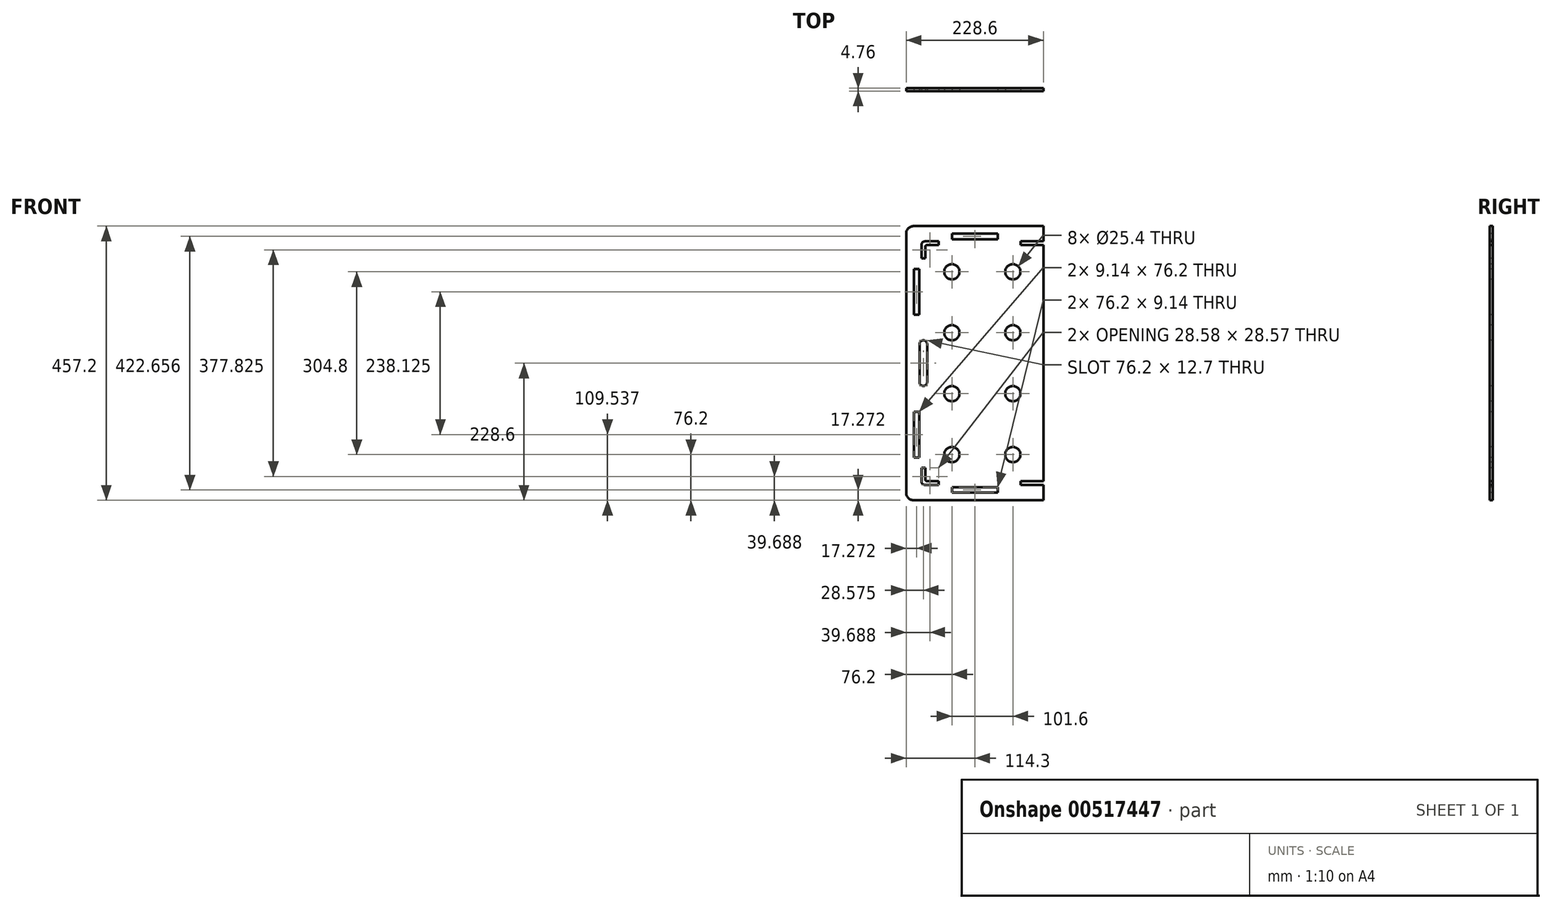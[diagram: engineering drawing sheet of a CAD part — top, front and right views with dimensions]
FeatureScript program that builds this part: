
annotation { "Feature Type Name" : "Feature", "Feature Type Description" : "" }
export const myFeature = defineFeature(function(context is Context, id is Id, definition is map)
    precondition{}
    {
        {
            var Q0;
            Q0=qCreatedBy(makeId("Front.planeOp"),FACE);
            var sketch = newSketch(context, id + "F0", { "sketchPlane" : qUnion([Q0])});
            skLineSegment(sketch, "E0.bottom", {"start": v(114.3, -228.6) * mm, "end": v(-101.6, -228.6) * mm});
            skLineSegment(sketch, "E0.top", {"start": v(114.3, 228.6) * mm, "end": v(-101.6, 228.6) * mm});
            skLineSegment(sketch, "E0.left", {"start": v(114.3, -228.6) * mm, "end": v(114.3, 228.6) * mm});
            skLineSegment(sketch, "E0.right", {"start": v(-114.3, -215.9) * mm, "end": v(-114.3, 215.9) * mm});
            skPoint(sketch, "E0.middle", {"position": v(0, 0) * mm});
            skPoint(sketch, "E1.visualSharp", {"position": v(-114.3, 228.6) * mm});
            skArc(sketch, "E1.filletArc", {"start": v(-101.6, 228.6) * mm, "mid": v(-110.58, 224.88) * mm, "end": v(-114.3, 215.9) * mm});
            skPoint(sketch, "E2.visualSharp", {"position": v(-114.3, -228.6) * mm});
            skArc(sketch, "E2.filletArc", {"start": v(-114.3, -215.9) * mm, "mid": v(-110.58, -224.88) * mm, "end": v(-101.6, -228.6) * mm});
            skSolve(sketch);
        }
        {
            var Q0;
            Q0 = qSketchRegion(id + "F0", true);
            extrude(context, id + "F1", {"entities" : qUnion([Q0]), "depth" : 4.76 * mm, "offsetDistance" : 25.4 * mm});
        }
        {
            var Q0;
            Q0=makeQuery(id+"F1.opExtrude","CAP_FACE",FACE,{"disambiguationData":[OSD([sQuery(id+"F0.wireOp",EDGE,"E0.bottom"),sQuery(id+"F0.wireOp",EDGE,"E0.top"),sQuery(id+"F0.wireOp",EDGE,"E0.left"),sQuery(id+"F0.wireOp",EDGE,"E0.right")])],"isStart":false});
            var sketch = newSketch(context, id + "F2", { "sketchPlane" : qUnion([Q0])});
            skLineSegment(sketch, "E3.MirrorCS", {"start": v(-38.1, -215.9) * mm, "end": v(-38.1, -206.76) * mm});
            skLineSegment(sketch, "E4.MirrorCS", {"start": v(38.1, -215.9) * mm, "end": v(38.1, -206.76) * mm});
            skCircle(sketch, "E5", {"center": v(-38.1, 152.4) * mm, "radius": 12.7 * mm});
            skCircle(sketch, "E6.0.1.0", {"center": v(-38.1, 50.8) * mm, "radius": 12.7 * mm});
            skCircle(sketch, "E6.1.0.0", {"center": v(63.5, 152.4) * mm, "radius": 12.7 * mm});
            skCircle(sketch, "E6.1.1.0", {"center": v(63.5, 50.8) * mm, "radius": 12.7 * mm});
            skLineSegment(sketch, "E6.direction1", {"start": v(-38.1, 152.4) * mm, "end": v(63.5, 152.4) * mm, "construction": true});
            skLineSegment(sketch, "E6.direction2", {"start": v(-38.1, 152.4) * mm, "end": v(-38.1, 50.8) * mm, "construction": true});
            skLineSegment(sketch, "E7", {"start": v(-114.3, 0) * mm, "end": v(114.3, 0) * mm, "construction": true});
            skLineSegment(sketch, "E8.MirrorCS", {"start": v(-92.46, -80.96) * mm, "end": v(-101.6, -80.96) * mm});
            skLineSegment(sketch, "E9.MirrorCS", {"start": v(-92.46, -157.16) * mm, "end": v(-101.6, -157.16) * mm});
            skLineSegment(sketch, "E10.MirrorCS", {"start": v(-101.6, -157.16) * mm, "end": v(-101.6, -80.96) * mm});
            skLineSegment(sketch, "E11", {"start": v(6.35, 228.6) * mm, "end": v(6.35, -228.6) * mm, "construction": true});
            skLineSegment(sketch, "E12.trimOffspring", {"start": v(-38.1, -206.76) * mm, "end": v(38.1, -206.76) * mm});
            skLineSegment(sketch, "E13.trimOffspring", {"start": v(-38.1, -215.9) * mm, "end": v(38.1, -215.9) * mm});
            skLineSegment(sketch, "E14.bottom", {"start": v(114.3, -203.2) * mm, "end": v(76.2, -203.2) * mm});
            skLineSegment(sketch, "E14.top", {"start": v(114.3, -196.85) * mm, "end": v(76.2, -196.85) * mm});
            skLineSegment(sketch, "E14.left", {"start": v(114.3, -203.2) * mm, "end": v(114.3, -196.85) * mm});
            skLineSegment(sketch, "E14.right", {"start": v(76.2, -203.2) * mm, "end": v(76.2, -196.85) * mm});
            skLineSegment(sketch, "E15.bottom", {"start": v(-82.55, -203.2) * mm, "end": v(-60.32, -203.2) * mm});
            skLineSegment(sketch, "E15.top", {"start": v(-79.37, -196.85) * mm, "end": v(-60.32, -196.85) * mm});
            skLineSegment(sketch, "E15.right", {"start": v(-60.32, -203.2) * mm, "end": v(-60.32, -196.85) * mm});
            skLineSegment(sketch, "E16.top", {"start": v(-88.9, -174.63) * mm, "end": v(-82.55, -174.63) * mm});
            skLineSegment(sketch, "E16.left", {"start": v(-88.9, -196.85) * mm, "end": v(-88.9, -174.63) * mm});
            skLineSegment(sketch, "E16.right", {"start": v(-82.55, -193.68) * mm, "end": v(-82.55, -174.63) * mm});
            skCircle(sketch, "E17.MirrorC", {"center": v(-38.1, -50.8) * mm, "radius": 12.7 * mm});
            skCircle(sketch, "E18.MirrorC", {"center": v(63.5, -50.8) * mm, "radius": 12.7 * mm});
            skCircle(sketch, "E19.MirrorC", {"center": v(-38.1, -152.4) * mm, "radius": 12.7 * mm});
            skCircle(sketch, "E20.MirrorC", {"center": v(63.5, -152.4) * mm, "radius": 12.7 * mm});
            skLineSegment(sketch, "E21.bottom", {"start": v(-85.72, -38.1) * mm, "end": v(-85.72, -38.1) * mm});
            skLineSegment(sketch, "E21.right", {"start": v(-79.38, -31.75) * mm, "end": v(-79.38, 31.75) * mm});
            skLineSegment(sketch, "E22", {"start": v(-85.72, 38.1) * mm, "end": v(-85.72, 38.1) * mm});
            skLineSegment(sketch, "E23.trimOffspring", {"start": v(-92.07, -31.75) * mm, "end": v(-92.07, 31.75) * mm});
            skPoint(sketch, "E24.visualSharp", {"position": v(-92.07, 38.1) * mm});
            skArc(sketch, "E24.filletArc", {"start": v(-85.72, 38.1) * mm, "mid": v(-90.22, 36.24) * mm, "end": v(-92.07, 31.75) * mm});
            skPoint(sketch, "E25.visualSharp", {"position": v(-79.38, 38.1) * mm});
            skArc(sketch, "E25.filletArc", {"start": v(-79.37, 31.75) * mm, "mid": v(-81.23, 36.24) * mm, "end": v(-85.72, 38.1) * mm});
            skPoint(sketch, "E26.visualSharp", {"position": v(-79.38, -38.1) * mm});
            skArc(sketch, "E26.filletArc", {"start": v(-85.72, -38.1) * mm, "mid": v(-81.23, -36.24) * mm, "end": v(-79.37, -31.75) * mm});
            skPoint(sketch, "E27.visualSharp", {"position": v(-92.08, -38.1) * mm});
            skArc(sketch, "E27.filletArc", {"start": v(-92.07, -31.75) * mm, "mid": v(-90.22, -36.24) * mm, "end": v(-85.72, -38.1) * mm});
            skLineSegment(sketch, "E28", {"start": v(-92.46, -80.96) * mm, "end": v(-92.46, -157.16) * mm});
            skLineSegment(sketch, "E29.MirrorCS", {"start": v(-92.46, 80.96) * mm, "end": v(-101.6, 80.96) * mm});
            skLineSegment(sketch, "E30.MirrorCS", {"start": v(-92.46, 157.16) * mm, "end": v(-101.6, 157.16) * mm});
            skLineSegment(sketch, "E31.MirrorCS", {"start": v(-101.6, 157.16) * mm, "end": v(-101.6, 80.96) * mm});
            skLineSegment(sketch, "E32.MirrorCS", {"start": v(-92.46, 80.96) * mm, "end": v(-92.46, 157.16) * mm});
            skLineSegment(sketch, "E33.MirrorCS", {"start": v(76.2, 203.2) * mm, "end": v(76.2, 196.85) * mm});
            skLineSegment(sketch, "E34.MirrorCS", {"start": v(6.35, -228.6) * mm, "end": v(6.35, 228.6) * mm, "construction": true});
            skLineSegment(sketch, "E35.MirrorCS", {"start": v(-38.1, 206.76) * mm, "end": v(38.1, 206.76) * mm});
            skLineSegment(sketch, "E36.MirrorCS", {"start": v(38.1, 215.9) * mm, "end": v(38.1, 206.76) * mm});
            skLineSegment(sketch, "E37.MirrorCS", {"start": v(114.3, 203.2) * mm, "end": v(76.2, 203.2) * mm});
            skLineSegment(sketch, "E38.MirrorCS", {"start": v(114.3, 203.2) * mm, "end": v(114.3, 196.85) * mm});
            skLineSegment(sketch, "E39.MirrorCS", {"start": v(-38.1, 215.9) * mm, "end": v(38.1, 215.9) * mm});
            skLineSegment(sketch, "E40.MirrorCS", {"start": v(-38.1, 215.9) * mm, "end": v(-38.1, 206.76) * mm});
            skLineSegment(sketch, "E41.MirrorCS", {"start": v(114.3, 196.85) * mm, "end": v(76.2, 196.85) * mm});
            skPoint(sketch, "E42.visualSharp", {"position": v(-88.9, -203.2) * mm});
            skArc(sketch, "E42.filletArc", {"start": v(-88.9, -196.85) * mm, "mid": v(-87.04, -201.34) * mm, "end": v(-82.55, -203.2) * mm});
            skArc(sketch, "E43.filletArc", {"start": v(-82.55, -193.68) * mm, "mid": v(-81.62, -195.92) * mm, "end": v(-79.37, -196.85) * mm});
            skArc(sketch, "E44.MirrorCS", {"start": v(-82.55, 193.68) * mm, "mid": v(-81.62, 195.92) * mm, "end": v(-79.37, 196.85) * mm});
            skLineSegment(sketch, "E45.MirrorCS", {"start": v(-79.37, 196.85) * mm, "end": v(-60.32, 196.85) * mm});
            skLineSegment(sketch, "E46.MirrorCS", {"start": v(-88.9, 196.85) * mm, "end": v(-88.9, 174.63) * mm});
            skArc(sketch, "E47.MirrorCS", {"start": v(-88.9, 196.85) * mm, "mid": v(-87.04, 201.34) * mm, "end": v(-82.55, 203.2) * mm});
            skLineSegment(sketch, "E48.MirrorCS", {"start": v(-82.55, 203.2) * mm, "end": v(-60.32, 203.2) * mm});
            skLineSegment(sketch, "E49.MirrorCS", {"start": v(-82.55, 193.68) * mm, "end": v(-82.55, 174.63) * mm});
            skLineSegment(sketch, "E50.MirrorCS", {"start": v(-60.32, 203.2) * mm, "end": v(-60.32, 196.85) * mm});
            skLineSegment(sketch, "E51.MirrorCS", {"start": v(-88.9, 174.63) * mm, "end": v(-82.55, 174.63) * mm});
            skPoint(sketch, "E52.MirrorP", {"position": v(-88.9, 203.2) * mm});
            skPoint(sketch, "E53", {"position": v(76.2, -200.03) * mm});
            skPoint(sketch, "E54", {"position": v(-60.32, -200.03) * mm});
            skPoint(sketch, "E55", {"position": v(-85.72, -174.63) * mm});
            skSolve(sketch);
        }
        {
            var Q0;
            Q0 = qSketchRegion(id + "F2", true);
            extrude(context, id + "F3", {"entities" : qUnion([Q0]), "operationType" : NewBodyOperationType.REMOVE, "endBound" : BoundingType.THROUGH_ALL, "oppositeDirection" : true, "depth" : 25.4 * mm, "offsetDistance" : 25.4 * mm});
        }
    });
